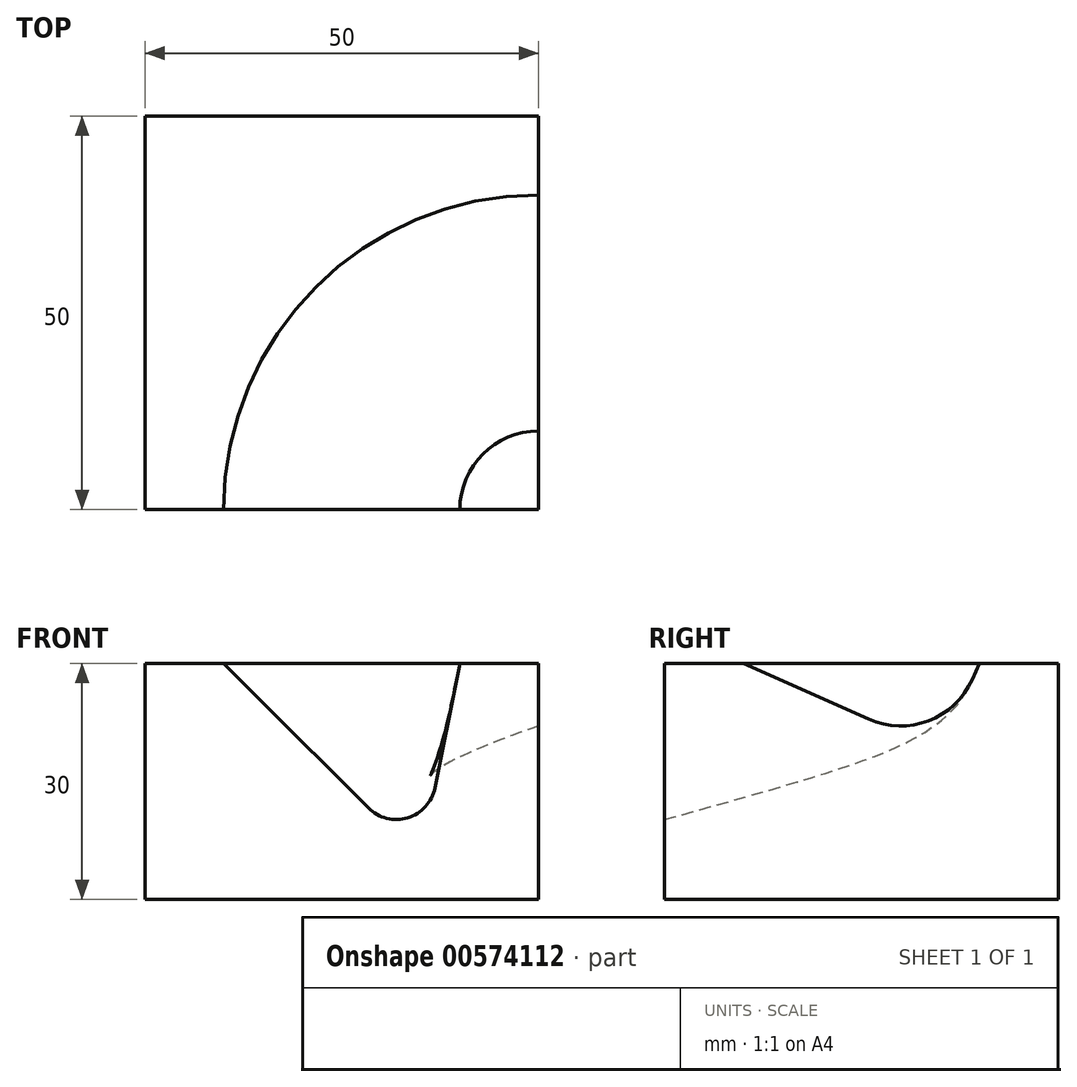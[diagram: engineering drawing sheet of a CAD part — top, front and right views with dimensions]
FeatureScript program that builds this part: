
annotation { "Feature Type Name" : "Feature", "Feature Type Description" : "" }
export const myFeature = defineFeature(function(context is Context, id is Id, definition is map)
    precondition{}
    {
        {
            var Q0;
            Q0=qCreatedBy(makeId("Top.planeOp"),FACE);
            var sketch = newSketch(context, id + "F0", { "sketchPlane" : qUnion([Q0])});
            skLineSegment(sketch, "E0.bottom", {"start": v(25, -25) * mm, "end": v(-25, -25) * mm});
            skLineSegment(sketch, "E0.top", {"start": v(25, 25) * mm, "end": v(-25, 25) * mm});
            skLineSegment(sketch, "E0.left", {"start": v(25, -25) * mm, "end": v(25, 25) * mm});
            skLineSegment(sketch, "E0.right", {"start": v(-25, -25) * mm, "end": v(-25, 25) * mm});
            skPoint(sketch, "E0.middle", {"position": v(0, 0) * mm});
            skSolve(sketch);
        }
        {
            var Q0;
            Q0=makeQuery(id+"F0.imprint","IMPRINT",FACE,{"disambiguationData":[TD([[makeQuery(id+"F0.imprint","IMPRINT",EDGE,{"derivedFrom":sQuery(id+"F0.wireOp",EDGE,"E0.bottom")}),-1.0]])]});
            extrude(context, id + "F1", {"entities" : qUnion([Q0]), "depth" : 15 * mm, "offsetDistance" : 25 * mm, "hasSecondDirection" : true, "secondDirectionOppositeDirection" : true, "secondDirectionDepth" : 15 * mm});
        }
        {
            var Q0;
            Q0=makeQuery(id+"F1.opExtrude","CAP_FACE",FACE,{"disambiguationData":[OSD([sQuery(id+"F0.wireOp",EDGE,"E0.bottom"),sQuery(id+"F0.wireOp",EDGE,"E0.top"),sQuery(id+"F0.wireOp",EDGE,"E0.left"),sQuery(id+"F0.wireOp",EDGE,"E0.right")])],"isStart":false});
            var sketch = newSketch(context, id + "F2", { "sketchPlane" : qUnion([Q0])});
            skArc(sketch, "E1", {"start": v(15, -25) * mm, "mid": v(17.93, -17.93) * mm, "end": v(25, -15) * mm});
            skSolve(sketch);
        }
        {
            var Q0;
            {var subQ2=sQuery(id+"F2.wireOp",EDGE,"E1");Q0=makeQuery(id+"F2.imprint","IMPRINT",FACE,{"disambiguationData":[TD([[makeQuery(id+"F2.imprint","IMPRINT",EDGE,{"derivedFrom":subQ2}),1.0]])]});}
            var sketch = newSketch(context, id + "F3", { "sketchPlane" : qUnion([Q0])});
            skArc(sketch, "E2", {"start": v(-15, -25) * mm, "mid": v(-3.28, 3.28) * mm, "end": v(25, 15) * mm});
            skSolve(sketch);
        }
        {
            var Q0;
            Q0=makeQuery(id+"F1.opExtrude","SWEPT_FACE",FACE,{"disambiguationData":[OSD([sQuery(id+"F0.wireOp",EDGE,"E0.bottom")])]});
            var sketch = newSketch(context, id + "F4", { "sketchPlane" : qUnion([Q0])});
            skLineSegment(sketch, "E3", {"start": v(-15, 15) * mm, "end": v(3.4, -3.4) * mm});
            skLineSegment(sketch, "E4", {"start": v(11.83, -0.84) * mm, "end": v(15, 15) * mm});
            skPoint(sketch, "E5.visualSharp", {"position": v(10, -10) * mm});
            skArc(sketch, "E5.filletArc", {"start": v(3.4, -3.4) * mm, "mid": v(8.38, -4.64) * mm, "end": v(11.83, -0.84) * mm});
            skSolve(sketch);
        }
        {
            var Q0;
            Q0=makeQuery(id+"F1.opExtrude","SWEPT_FACE",FACE,{"disambiguationData":[OSD([sQuery(id+"F0.wireOp",EDGE,"E0.left")])]});
            var sketch = newSketch(context, id + "F5", { "sketchPlane" : qUnion([Q0])});
            skLineSegment(sketch, "E6", {"start": v(-15, 15) * mm, "end": v(0.87, 7.9) * mm});
            skLineSegment(sketch, "E7", {"start": v(14.08, 12.95) * mm, "end": v(15, 15) * mm});
            skPoint(sketch, "E8.visualSharp", {"position": v(10, 3.82) * mm});
            skArc(sketch, "E8.filletArc", {"start": v(0.87, 7.9) * mm, "mid": v(8.52, 7.69) * mm, "end": v(14.08, 12.95) * mm});
            skSolve(sketch);
        }
        {
            var Q1;
            {var subQ0=sQuery(id+"F4.wireOp",EDGE,"E3");Q1=makeQuery(id+"F4.imprint","IMPRINT",FACE,{"disambiguationData":[TD([[makeQuery(id+"F4.imprint","IMPRINT",EDGE,{"derivedFrom":subQ0}),1.0]])]});}
            var Q2;
            {var subQ0=sQuery(id+"F5.wireOp",EDGE,"E6");Q2=makeQuery(id+"F5.imprint","IMPRINT",FACE,{"disambiguationData":[TD([[makeQuery(id+"F5.imprint","IMPRINT",EDGE,{"derivedFrom":subQ0}),1.0]])]});}
            var Q3;
            Q3=sQuery(id+"F3.wireOp",EDGE,"E2");
            var Q4;
            Q4=sQuery(id+"F2.wireOp",EDGE,"E1");
            loft(context, id + "F6", {"operationType" : NewBodyOperationType.REMOVE, "addGuides" : true, "sheetProfilesArray" : [{ "sheetProfileEntities" : qUnion([Q1]) }, { "sheetProfileEntities" : qUnion([Q2]) }], "guidesArray" : [{ "guideEntities" : qUnion([Q3]), "guideDerivativeType" : LoftGuideDerivativeType.DEFAULT, "guideDerivativeMagnitude" : 1 }, { "guideEntities" : qUnion([Q4]), "guideDerivativeType" : LoftGuideDerivativeType.DEFAULT, "guideDerivativeMagnitude" : 1 }]});
        }
    });
